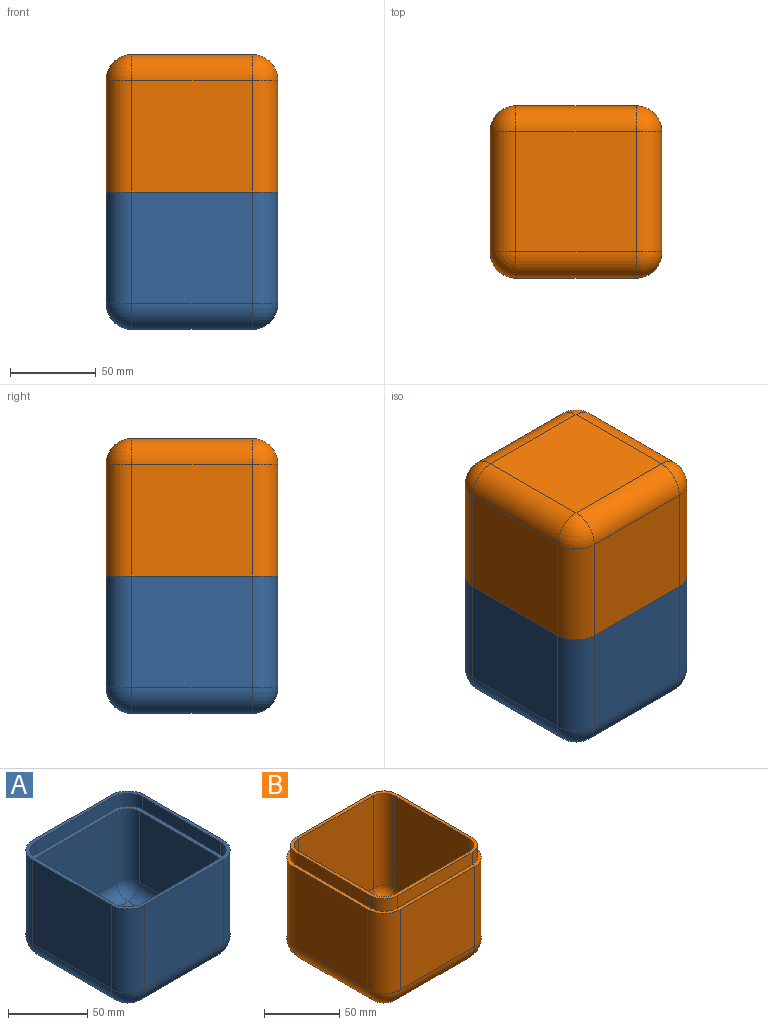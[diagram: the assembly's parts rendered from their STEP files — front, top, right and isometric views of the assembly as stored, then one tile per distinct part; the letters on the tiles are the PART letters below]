
ASSEMBLY  parts=2 mates=1
PART A: 44 faces, bbox 100x100x80 mm
  f0: plane 100x100mm, normal (0,0,1), area 916mm2, adj f1,f2,f3,f4,f6,f8,f11,f17
  f1: plane 70x65mm, normal (-1,0,0), area 4550mm2, adj f0,f11,f15,f17
  f2: plane 70x65mm, normal (0,-1,0), area 4550mm2, adj f0,f8,f14,f17
  f3: plane 70x65mm, normal (1,0,0), area 4550mm2, adj f0,f6,f8,f9
  f4: plane 70x65mm, normal (0,1,0), area 4550mm2, adj f0,f6,f10,f11
  f5: plane 70x70mm, normal (0,0,-1), area 4900mm2, adj f9,f10,f14,f15
  f6: cylinder r=15mm len=65mm, axis (0,0,-1), area 1531.5mm2, adj f0,f3,f4,f7
  f7: sphere r=15mm, area 353.4mm2, adj f6,f9,f10
  f8: cylinder r=15mm len=65mm, axis (0,0,1), area 1531.5mm2, adj f0,f2,f3,f12
  f9: cylinder r=15mm len=70mm, axis (0,1,0), area 1649.3mm2, adj f3,f5,f7,f12
  f10: cylinder r=15mm len=70mm, axis (-1,0,0), area 1649.3mm2, adj f4,f5,f7,f13
  f11: cylinder r=15mm len=65mm, axis (0,0,1), area 1531.5mm2, adj f0,f1,f4,f13
  f12: sphere r=15mm, area 353.4mm2, adj f8,f9,f14
  f13: sphere r=15mm, area 353.4mm2, adj f10,f11,f15
  f14: cylinder r=15mm len=70mm, axis (1,0,0), area 1649.3mm2, adj f2,f5,f12,f16
  f15: cylinder r=15mm len=70mm, axis (0,-1,0), area 1649.3mm2, adj f1,f5,f13,f16
  f16: sphere r=15mm, area 353.4mm2, adj f14,f15,f17
  f17: cylinder r=15mm len=65mm, axis (0,0,-1), area 1531.5mm2, adj f0,f1,f2,f16
  f18: plane 95x95mm, normal (0,0,1), area 876.7mm2, adj f19,f20,f21,f22,f23,f24,f25,f26
  f19: plane 70x10mm, normal (-1,0,0), area 700mm2, adj f0,f18,f20,f26
  f20: cylinder r=12.5mm len=12.5mm, axis (0,0,1), area 196.3mm2, adj f0,f18,f19,f21
  f21: plane 70x10mm, normal (0,-1,0), area 700mm2, adj f0,f18,f20,f22
  f22: cylinder r=12.5mm len=12.5mm, axis (0,0,1), area 196.3mm2, adj f0,f18,f21,f23
  f23: plane 70x10mm, normal (1,0,0), area 700mm2, adj f0,f18,f22,f24
  f24: cylinder r=12.5mm len=12.5mm, axis (0,0,1), area 196.3mm2, adj f0,f18,f23,f25
  f25: plane 70x10mm, normal (0,1,0), area 700mm2, adj f0,f18,f24,f26
  f26: cylinder r=12.5mm len=12.5mm, axis (0,0,1), area 196.3mm2, adj f0,f18,f19,f25
  f27: plane 70x70mm, normal (0,0,1), area 4900mm2, adj f28,f29,f30,f31
  f28: cylinder r=10mm len=70mm, axis (0,-1,0), area 1099.6mm2, adj f27,f34,f35,f43
  f29: cylinder r=10mm len=70mm, axis (1,0,0), area 1099.6mm2, adj f27,f33,f35,f42
  f30: cylinder r=10mm len=70mm, axis (0,1,0), area 1099.6mm2, adj f27,f32,f33,f40
  f31: cylinder r=10mm len=70mm, axis (-1,0,0), area 1099.6mm2, adj f27,f32,f34,f39
  f32: sphere r=10mm, area 157.1mm2, adj f30,f31,f37
  f33: sphere r=10mm, area 157.1mm2, adj f29,f30,f36
  f34: sphere r=10mm, area 157.1mm2, adj f28,f31,f38
  f35: sphere r=10mm, area 157.1mm2, adj f28,f29,f41
  f36: cylinder r=10mm len=55mm, axis (0,0,1), area 863.9mm2, adj f18,f33,f40,f42
  f37: cylinder r=10mm len=55mm, axis (0,0,-1), area 863.9mm2, adj f18,f32,f39,f40
  f38: cylinder r=10mm len=55mm, axis (0,0,1), area 863.9mm2, adj f18,f34,f39,f43
  f39: plane 70x55mm, normal (0,-1,0), area 3850mm2, adj f18,f31,f37,f38
  f40: plane 70x55mm, normal (-1,0,0), area 3850mm2, adj f18,f30,f36,f37
  f41: cylinder r=10mm len=55mm, axis (0,0,-1), area 863.9mm2, adj f18,f35,f42,f43
  f42: plane 70x55mm, normal (0,1,0), area 3850mm2, adj f18,f29,f36,f41
  f43: plane 70x55mm, normal (1,0,0), area 3850mm2, adj f18,f28,f38,f41
PART B: 44 faces, bbox 100x100x90 mm
  f0: plane 70x65mm, normal (-1,0,0), area 4550mm2, adj f4,f11,f15,f17
  f1: plane 70x65mm, normal (0,-1,0), area 4550mm2, adj f4,f8,f14,f17
  f2: plane 70x65mm, normal (1,0,0), area 4550mm2, adj f4,f6,f8,f9
  f3: plane 70x65mm, normal (0,1,0), area 4550mm2, adj f4,f6,f10,f11
  f4: plane 100x100mm, normal (0,0,1), area 916mm2, adj f0,f1,f2,f3,f6,f8,f11,f17
  f5: plane 70x70mm, normal (0,0,-1), area 4900mm2, adj f9,f10,f14,f15
  f6: cylinder r=15mm len=65mm, axis (0,0,-1), area 1531.5mm2, adj f2,f3,f4,f7
  f7: sphere r=15mm, area 353.4mm2, adj f6,f9,f10
  f8: cylinder r=15mm len=65mm, axis (0,0,1), area 1531.5mm2, adj f1,f2,f4,f12
  f9: cylinder r=15mm len=70mm, axis (0,1,0), area 1649.3mm2, adj f2,f5,f7,f12
  f10: cylinder r=15mm len=70mm, axis (-1,0,0), area 1649.3mm2, adj f3,f5,f7,f13
  f11: cylinder r=15mm len=65mm, axis (0,0,1), area 1531.5mm2, adj f0,f3,f4,f13
  f12: sphere r=15mm, area 353.4mm2, adj f8,f9,f14
  f13: sphere r=15mm, area 353.4mm2, adj f10,f11,f15
  f14: cylinder r=15mm len=70mm, axis (1,0,0), area 1649.3mm2, adj f1,f5,f12,f16
  f15: cylinder r=15mm len=70mm, axis (0,-1,0), area 1649.3mm2, adj f0,f5,f13,f16
  f16: sphere r=15mm, area 353.4mm2, adj f14,f15,f17
  f17: cylinder r=15mm len=65mm, axis (0,0,-1), area 1531.5mm2, adj f0,f1,f4,f16
  f18: cylinder r=12.5mm len=12.5mm, axis (0,0,-1), area 196.3mm2, adj f4,f19,f25,f26
  f19: plane 70x10mm, normal (-1,0,0), area 700mm2, adj f4,f18,f20,f26
  f20: cylinder r=12.5mm len=12.5mm, axis (0,0,-1), area 196.3mm2, adj f4,f19,f21,f26
  f21: plane 70x10mm, normal (0,-1,0), area 700mm2, adj f4,f20,f22,f26
  f22: cylinder r=12.5mm len=12.5mm, axis (0,0,-1), area 196.3mm2, adj f4,f21,f23,f26
  f23: plane 70x10mm, normal (1,0,0), area 700mm2, adj f4,f22,f24,f26
  f24: cylinder r=12.5mm len=12.5mm, axis (0,0,-1), area 196.3mm2, adj f4,f23,f25,f26
  f25: plane 70x10mm, normal (0,1,0), area 700mm2, adj f4,f18,f24,f26
  f26: plane 95x95mm, normal (0,0,1), area 876.7mm2, adj f18,f19,f20,f21,f22,f23,f24,f25
  f27: plane 70x70mm, normal (0,0,1), area 4900mm2, adj f28,f30,f32,f34
  f28: cylinder r=10mm len=70mm, axis (0,-1,0), area 1099.6mm2, adj f27,f29,f35,f43
  f29: sphere r=10mm, area 157.1mm2, adj f28,f30,f42
  f30: cylinder r=10mm len=70mm, axis (-1,0,0), area 1099.6mm2, adj f27,f29,f31,f41
  f31: sphere r=10mm, area 157.1mm2, adj f30,f32,f40
  f32: cylinder r=10mm len=70mm, axis (0,1,0), area 1099.6mm2, adj f27,f31,f33,f39
  f33: sphere r=10mm, area 157.1mm2, adj f32,f34,f38
  f34: cylinder r=10mm len=70mm, axis (1,0,0), area 1099.6mm2, adj f27,f33,f35,f37
  f35: sphere r=10mm, area 157.1mm2, adj f28,f34,f36
  f36: cylinder r=10mm len=75mm, axis (0,0,-1), area 1178.1mm2, adj f26,f35,f37,f43
  f37: plane 75x70mm, normal (0,1,0), area 5250mm2, adj f26,f34,f36,f38
  f38: cylinder r=10mm len=75mm, axis (0,0,1), area 1178.1mm2, adj f26,f33,f37,f39
  f39: plane 75x70mm, normal (-1,0,0), area 5250mm2, adj f26,f32,f38,f40
  f40: cylinder r=10mm len=75mm, axis (0,0,-1), area 1178.1mm2, adj f26,f31,f39,f41
  f41: plane 75x70mm, normal (0,-1,0), area 5250mm2, adj f26,f30,f40,f42
  f42: cylinder r=10mm len=75mm, axis (0,0,1), area 1178.1mm2, adj f26,f29,f41,f43
  f43: plane 75x70mm, normal (1,0,0), area 5250mm2, adj f26,f28,f36,f42
PLACE A t=(-0.36,0.19,-39.39)mm
PLACE B rot(axis=(0,1,0),180deg) t=(-0.36,0.19,120.61)mm
MATE fastened B.f19 <-> A.f19  axis (1,0,0) through (47.14,0.19,35.61)mm
